# Revit family: Legrand_Autotransformateurs
name_source: partatom
category: Installations électriques
revit_build: Autodesk Revit 2018 (Build: 20170223_1515(x64)
units: mm (PartAtom-declared; Revit-internal decimal feet)

## family parameters
Basée sur le plan de construction = Non
Conserver l'orientation des annotations = Non
Cote de connecteur circulaire = Utiliser le diamètre
Couper avec des vides une fois chargée = Non
Numéro OmniClass = 23.80.00.00
Partagée = Non
Point de calcul de pièce = Non
Titre OmniClass = Electric Power and Lighting
Toujours verticalement = Oui
Type d'élément = Normal

## types (14) — shared parameters
Fabricant = Legrand
Modèle = Triphasés IP21
Tension d'utilisation = 400-230 V ou 230-400 V par réversibilité compensée jusqu’à 16 kVA
URL = www.legrand.com

## per-type parameters (varying)
| type | 042198 | 042199, 042200, 042201 | 042202 | 042203, 042204, 042205 | 042206 | 042207 | 142190, 142191 | 142208, 142209 | Conditions Générale d'Utilisation | Poids | Section câble primaire | Section câble secondaire | Ucc (%) | diamètre de fixation | dimension A | dimension B | dimension C | fixation F | fixation G | perte totale max | perte à vide | puissance |
| Autotransformateur triphasé 142208 | Non | Non | Non | Non | Non | Non | Non | Oui | https://export.legrand.com | 176.00 kg | 70 mm² | 70 mm² | 1.6 | 11 mm  [stored 0.0360892 ft] | 590 mm  [stored 1.9357 ft] | 650 mm  [stored 2.13255 ft] | 500 mm  [stored 1.64042 ft] | 570 mm  [stored 1.87008 ft] | 166 mm  [stored 0.544619 ft] | 948 W | 210 W | 63 kVA |
| Autotransformateur triphasé 142209 | Non | Non | Non | Non | Non | Non | Non | Oui |  | 188.00 kg | 120 mm² | 120 mm² | 1.5 | 11 mm  [stored 0.0360892 ft] | 590 mm  [stored 1.9357 ft] | 650 mm  [stored 2.13255 ft] | 500 mm  [stored 1.64042 ft] | 570 mm  [stored 1.87008 ft] | 206 mm  [stored 0.675853 ft] | 1343 W | 341 W | 100 kVA |
| Autotransformateur triphasé 142190 | Non | Non | Non | Non | Non | Non | Oui | Non | https://export.legrand.com | 324.00 kg | 150 mm² | 150 mm² | 1.4 | 16 mm  [stored 0.0524934 ft] | 670 mm  [stored 2.19816 ft] | 700 mm  [stored 2.29659 ft] | 610 mm  [stored 2.00131 ft] | 400 mm  [stored 1.31234 ft] | 580 mm  [stored 1.90289 ft] | 1938 W | 602 W | 125 kVA |
| Autotransformateur triphasé 142191 | Non | Non | Non | Non | Non | Non | Oui | Non | https://export.legrand.com | 361.00 kg | 150 mm² | 150 mm² | 1.3 | 16 mm  [stored 0.0524934 ft] | 670 mm  [stored 2.19816 ft] | 700 mm  [stored 2.29659 ft] | 610 mm  [stored 2.00131 ft] | 400 mm  [stored 1.31234 ft] | 580 mm  [stored 1.90289 ft] | 2220 W | 670 W | 160 kVA |
| Autotransformateur triphasé 042198 | Oui | Non | Non | Non | Non | Non | Non | Non | https://export.legrand.com | 10.00 kg | 4 mm² | 4 mm² | 5.92 | 7 mm  [stored 0.0229659 ft] | 220 mm  [stored 0.721785 ft] | 220 mm  [stored 0.721785 ft] | 190 mm  [stored 0.62336 ft] | 200 mm  [stored 0.656168 ft] | 60 mm  [stored 0.19685 ft] | 51 W | 10 W | 1 kVA |
| Autotransformateur triphasé 042199 | Non | Oui | Non | Non | Non | Non | Non | Non | https://export.legrand.com | 11.00 kg | 4 mm² | 4 mm² | 4.7 | 7 mm  [stored 0.0229659 ft] | 240 mm  [stored 0.787402 ft] | 270 mm  [stored 0.885827 ft] | 190 mm  [stored 0.62336 ft] | 220 mm  [stored 0.721785 ft] | 60 mm  [stored 0.19685 ft] | 64 W | 13 W | 1 kVA |
| Autotransformateur triphasé 042200 | Non | Oui | Non | Non | Non | Non | Non | Non | https://export.legrand.com | 14.00 kg | 4 mm² | 4 mm² | 3.6 | 7 mm  [stored 0.0229659 ft] | 240 mm  [stored 0.787402 ft] | 270 mm  [stored 0.885827 ft] | 190 mm  [stored 0.62336 ft] | 220 mm  [stored 0.721785 ft] | 64 mm  [stored 0.209974 ft] | 82 W | 21 W | 2 kVA |
| Autotransformateur triphasé 042201 | Non | Oui | Non | Non | Non | Non | Non | Non | https://export.legrand.com | 20.00 kg | 6 mm² | 6 mm² | 2.6 | 7 mm  [stored 0.0229659 ft] | 240 mm  [stored 0.787402 ft] | 270 mm  [stored 0.885827 ft] | 190 mm  [stored 0.62336 ft] | 220 mm  [stored 0.721785 ft] | 86 mm  [stored 0.282152 ft] | 101 W | 34 W | 3 kVA |
| Autotransformateur triphasé 042202 | Non | Non | Oui | Non | Non | Non | Non | Non | https://export.legrand.com | 26.00 kg | 10 mm² | 10 mm² | 2.2 | 9 mm  [stored 0.0295276 ft] | 370 mm  [stored 1.21391 ft] | 330 mm  [stored 1.08268 ft] | 190 mm  [stored 0.62336 ft] | 350 mm  [stored 1.14829 ft] | 69 mm  [stored 0.226378 ft] | 132 W | 40 W | 4 kVA |
| Autotransformateur triphasé 042203 | Non | Non | Non | Oui | Non | Non | Non | Non | https://export.legrand.com | 28.50 kg | 10 mm² | 10 mm² | 3.4 | 9 mm  [stored 0.0295276 ft] | 420 mm  [stored 1.37795 ft] | 390 mm  [stored 1.27953 ft] | 310 mm  [stored 1.01706 ft] | 400 mm  [stored 1.31234 ft] | 86 mm  [stored 0.282152 ft] | 284 W | 59 W | 6 kVA |
| Autotransformateur triphasé 042204 | Non | Non | Non | Oui | Non | Non | Non | Non | https://export.legrand.com | 39.70 kg | 10 mm² | 10 mm² | 2.4 | 9 mm  [stored 0.0295276 ft] | 420 mm  [stored 1.37795 ft] | 390 mm  [stored 1.27953 ft] | 310 mm  [stored 1.01706 ft] | 400 mm  [stored 1.31234 ft] | 106 mm  [stored 0.347769 ft] | 332 W | 85 W | 10 kVA |
| Autotransformateur triphasé 042205 | Non | Non | Non | Oui | Non | Non | Non | Non | https://export.legrand.com | 53.00 kg | 35 mm² | 35 mm² | 1.8 | 9 mm  [stored 0.0295276 ft] | 420 mm  [stored 1.37795 ft] | 390 mm  [stored 1.27953 ft] | 310 mm  [stored 1.01706 ft] | 400 mm  [stored 1.31234 ft] | 126 mm  [stored 0.413386 ft] | 394 W | 112 W | 16 kVA |
| Autotransformateur triphasé 042206 | Non | Non | Non | Non | Oui | Non | Non | Non | https://export.legrand.com | 284.50 kg | 35 mm² | 35 mm² | 1.6 | 9 mm  [stored 0.0295276 ft] | 470 mm  [stored 1.54199 ft] | 410 mm  [stored 1.34514 ft] | 380 mm | 450 mm  [stored 1.47638 ft] | 146 mm  [stored 0.479003 ft] | 564 W | 200 W | 25 kVA |
| Autotransformateur triphasé 042207 | Non | Non | Non | Non | Non | Oui | Non | Non | https://export.legrand.com | 125.50 kg | 35 mm² | 35 mm² | 1.6 | 9 mm  [stored 0.0295276 ft] | 530 mm  [stored 1.73885 ft] | 460 mm  [stored 1.50919 ft] | 380 mm | 510 mm  [stored 1.67323 ft] | 146 mm  [stored 0.479003 ft] | 766 W | 265 W | 40 kVA |

note: [stored X ft] marks values corroborated as IEEE doubles in the binary element streams (Revit-internal decimal feet)
